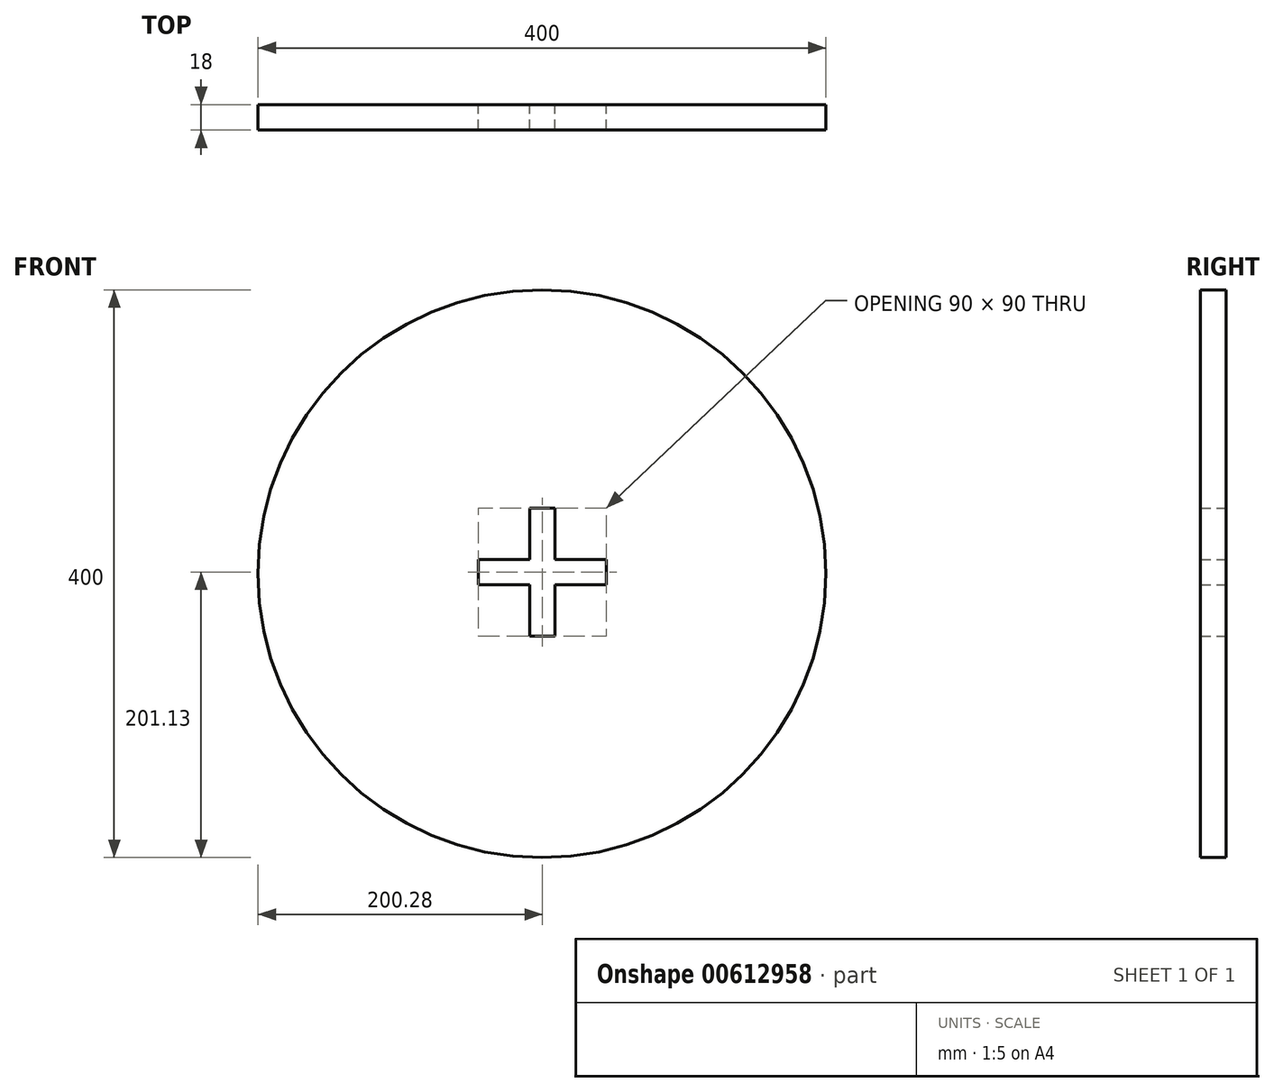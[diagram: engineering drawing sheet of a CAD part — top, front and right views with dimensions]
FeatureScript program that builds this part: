
annotation { "Feature Type Name" : "Feature", "Feature Type Description" : "" }
export const myFeature = defineFeature(function(context is Context, id is Id, definition is map)
    precondition{}
    {
        {
            var Q0;
            Q0=qCreatedBy(makeId("Front.planeOp"),FACE);
            var sketch = newSketch(context, id + "F0", { "sketchPlane" : qUnion([Q0])});
            skCircle(sketch, "E0", {"center": v(-0.28, -1.13) * mm, "radius": 200 * mm});
            skLineSegment(sketch, "E1.bottom", {"start": v(9, -45) * mm, "end": v(-9, -45) * mm});
            skLineSegment(sketch, "E1.top", {"start": v(9, 45) * mm, "end": v(-9, 45) * mm});
            skLineSegment(sketch, "E1.left", {"start": v(9, -45) * mm, "end": v(9, -9) * mm});
            skLineSegment(sketch, "E1.right", {"start": v(-9, -45) * mm, "end": v(-9, -9) * mm});
            skPoint(sketch, "E1.middle", {"position": v(0, 0) * mm});
            skLineSegment(sketch, "E2.bottom", {"start": v(45, -9) * mm, "end": v(9, -9) * mm});
            skLineSegment(sketch, "E2.top", {"start": v(45, 9) * mm, "end": v(9, 9) * mm});
            skLineSegment(sketch, "E2.left", {"start": v(45, -9) * mm, "end": v(45, 9) * mm});
            skLineSegment(sketch, "E2.right", {"start": v(-45, -9) * mm, "end": v(-45, 9) * mm});
            skLineSegment(sketch, "E3.trimOffspring", {"start": v(-9, 9) * mm, "end": v(-45, 9) * mm});
            skLineSegment(sketch, "E4.trimOffspring", {"start": v(-9, -9) * mm, "end": v(-45, -9) * mm});
            skLineSegment(sketch, "E5.trimOffspring", {"start": v(-9, 9) * mm, "end": v(-9, 45) * mm});
            skLineSegment(sketch, "E6.trimOffspring", {"start": v(9, 9) * mm, "end": v(9, 45) * mm});
            skSolve(sketch);
        }
        {
            var Q0;
            Q0=makeQuery(id+"F0.imprint","IMPRINT",FACE,{"disambiguationData":[TD([[makeQuery(id+"F0.imprint","IMPRINT",EDGE,{"derivedFrom":sQuery(id+"F0.wireOp",EDGE,"E0")}),1.0]])]});
            extrude(context, id + "F1", {"entities" : qUnion([Q0]), "depth" : 18 * mm, "offsetDistance" : 25 * mm});
        }
    });
